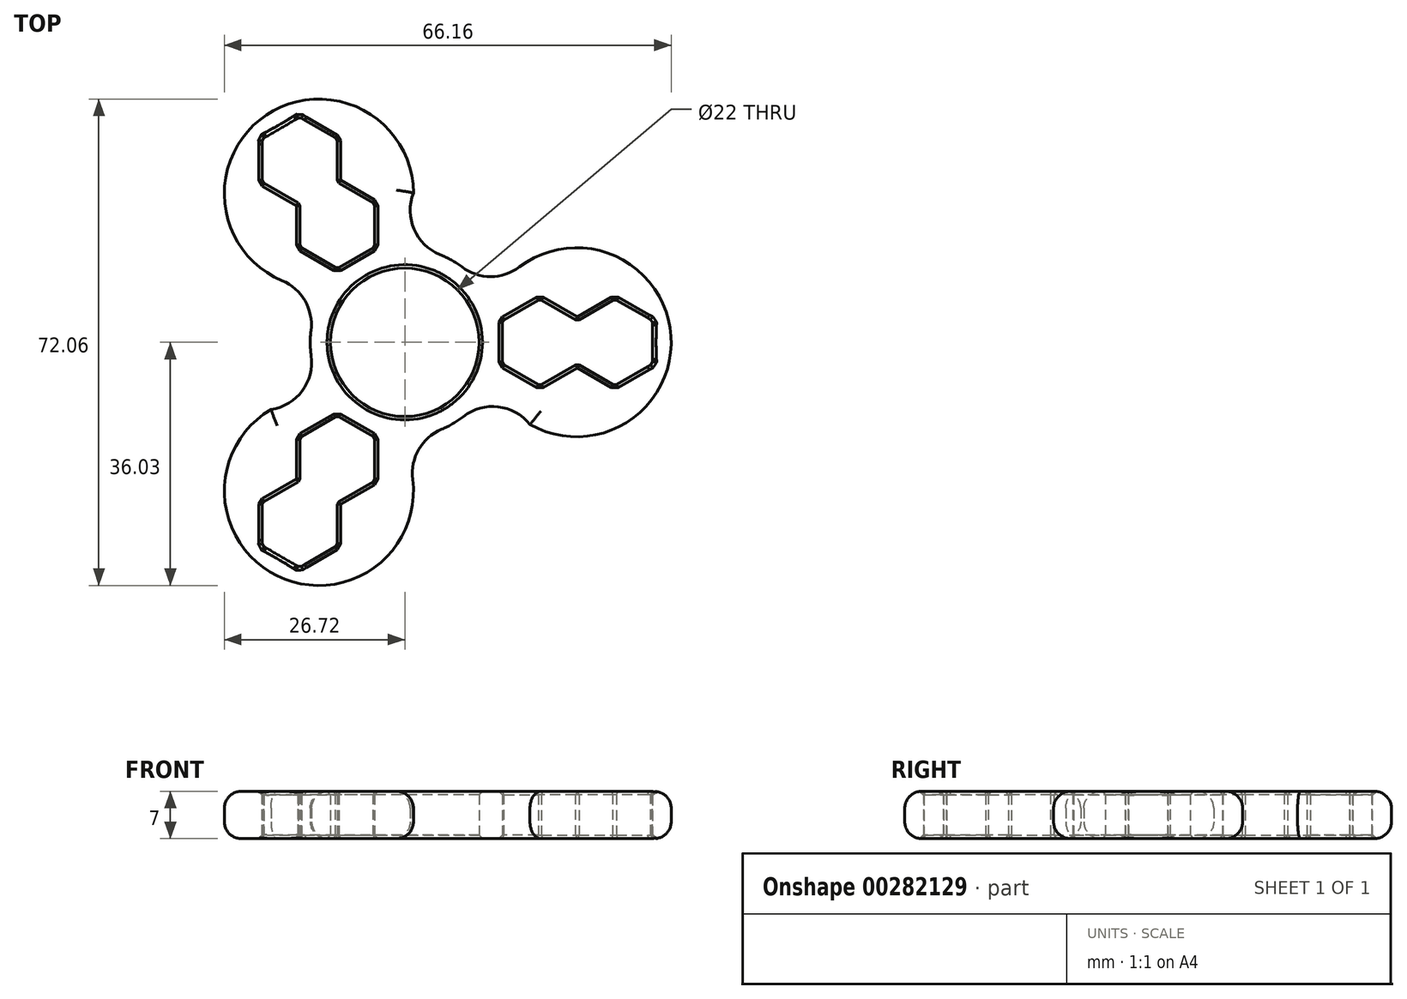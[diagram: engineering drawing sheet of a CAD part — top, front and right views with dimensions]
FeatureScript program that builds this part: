
annotation { "Feature Type Name" : "Feature", "Feature Type Description" : "" }
export const myFeature = defineFeature(function(context is Context, id is Id, definition is map)
    precondition{}
    {
        {
            var Q0;
            Q0=qCreatedBy(makeId("Top.planeOp"),FACE);
            var sketch = newSketch(context, id + "F0", { "sketchPlane" : qUnion([Q0])});
            skCircle(sketch, "E0", {"center": v(0, 0) * mm, "radius": 11 * mm});
            skCircle(sketch, "E1", {"center": v(0, 0) * mm, "radius": 14 * mm});
            skCircle(sketch, "E2", {"center": v(25.44, 0) * mm, "radius": 14 * mm});
            skArc(sketch, "E3", {"start": v(18.93, 13.42) * mm, "mid": v(12.38, 9.74) * mm, "end": v(6.21, 14.03) * mm});
            skArc(sketch, "E4.MirrorCS", {"start": v(19.21, -13.2) * mm, "mid": v(12.66, -9.52) * mm, "end": v(6.5, -13.81) * mm});
            skCircle(sketch, "E5.cCircle", {"center": v(31.1, 0) * mm, "radius": 6.4 * mm, "construction": true});
            skLineSegment(sketch, "E5.0", {"start": v(25.55, -3.2) * mm, "end": v(25.55, 3.2) * mm});
            skLineSegment(sketch, "E5.1", {"start": v(25.55, 3.2) * mm, "end": v(31.1, 6.4) * mm});
            skLineSegment(sketch, "E5.2", {"start": v(31.1, 6.4) * mm, "end": v(36.65, 3.2) * mm});
            skLineSegment(sketch, "E5.3", {"start": v(36.65, 3.2) * mm, "end": v(36.65, -3.2) * mm});
            skLineSegment(sketch, "E5.4", {"start": v(36.65, -3.2) * mm, "end": v(31.1, -6.4) * mm});
            skLineSegment(sketch, "E5.5", {"start": v(31.1, -6.4) * mm, "end": v(25.55, -3.2) * mm});
            skCircle(sketch, "E6.cCircle", {"center": v(20, 0) * mm, "radius": 6.4 * mm, "construction": true});
            skLineSegment(sketch, "E6.0", {"start": v(25.55, -3.2) * mm, "end": v(20, -6.4) * mm});
            skLineSegment(sketch, "E6.1", {"start": v(20, -6.4) * mm, "end": v(14.45, -3.2) * mm});
            skLineSegment(sketch, "E6.2", {"start": v(14.45, -3.2) * mm, "end": v(14.45, 3.2) * mm});
            skLineSegment(sketch, "E6.3", {"start": v(14.45, 3.2) * mm, "end": v(20, 6.4) * mm});
            skLineSegment(sketch, "E6.4", {"start": v(20, 6.4) * mm, "end": v(25.55, 3.2) * mm});
            skLineSegment(sketch, "E6.5", {"start": v(25.55, 3.2) * mm, "end": v(25.55, -3.2) * mm});
            skLineSegment(sketch, "E7", {"start": v(0, 0) * mm, "end": v(20, 0) * mm, "construction": true});
            skSolve(sketch);
        }
        {
            var Q0;
            Q0=makeQuery(id+"F0.imprint","IMPRINT",FACE,{"disambiguationData":[TD([[makeQuery(id+"F0.imprint","IMPRINT",EDGE,{"derivedFrom":sQuery(id+"F0.wireOp",EDGE,"E0")}),-1.0]])]});
            var Q1;
            {var subQ0=sQuery(id+"F0.wireOp",EDGE,"E2");var subQ1=sQuery(id+"F0.wireOp",EDGE,"E1");var subQ2=makeQuery(id+"F0.imprint","INTERSECT",VERTEX,{"disambiguationData":[OD(0.0)],"derivedFrom":[subQ1,subQ0]});Q1=makeQuery(id+"F0.imprint","IMPRINT",FACE,{"disambiguationData":[TD([[makeQuery(id+"F0.imprint","IMPRINT",EDGE,{"disambiguationData":[TD([[subQ2,1.0]])],"derivedFrom":subQ1}),1.0]])]});}
            var Q2;
            Q2=makeQuery(id+"F0.imprint","IMPRINT",FACE,{"disambiguationData":[TD([[makeQuery(id+"F0.imprint","IMPRINT",EDGE,{"derivedFrom":sQuery(id+"F0.wireOp",EDGE,"E5.1")}),1.0]])]});
            extrude(context, id + "F1", {"entities" : qUnion([Q0, Q1, Q2]), "endBound" : BoundingType.SYMMETRIC, "depth" : 7 * mm});
        }
        {
            var Q0;
            {var subQ0=sQuery(id+"F0.wireOp",EDGE,"E3");var subQ1=sQuery(id+"F0.wireOp",EDGE,"E1");var subQ2=makeQuery(id+"F0.imprint","INTERSECT",VERTEX,{"derivedFrom":[subQ1,subQ0]});Q0=makeQuery(id+"F0.imprint","IMPRINT",FACE,{"disambiguationData":[TD([[makeQuery(id+"F0.imprint","IMPRINT",EDGE,{"disambiguationData":[TD([[subQ2,1.0]])],"derivedFrom":subQ1}),-1.0]])]});}
            var Q1;
            Q1=makeQuery(id+"F0.imprint","IMPRINT",FACE,{"disambiguationData":[TD([[makeQuery(id+"F0.imprint","IMPRINT",EDGE,{"derivedFrom":sQuery(id+"F0.wireOp",EDGE,"UwXqT0ap-12Z3-Fupx-mhf0-3pL9q4EJ6cQW")}),-1.0]])]});
            var Q2;
            {var subQ0=sQuery(id+"F0.wireOp",EDGE,"gSAZEsJJ-cn3l-cjJ6-9HDa-52uPBN5IA6vx");Q2=makeQuery(id+"F0.imprint","IMPRINT",FACE,{"disambiguationData":[TD([[makeQuery(id+"F0.imprint","IMPRINT",EDGE,{"derivedFrom":subQ0}),1.0]])]});}
            var Q3;
            {var subQ0=sQuery(id+"F0.wireOp",EDGE,"VPdpeA7V-GjOX-LRlJ-2Vj8-VplDRYYToLq0");Q3=makeQuery(id+"F0.imprint","IMPRINT",FACE,{"disambiguationData":[TD([[makeQuery(id+"F0.imprint","IMPRINT",EDGE,{"derivedFrom":subQ0}),1.0]])]});}
            var Q4;
            {var subQ0=sQuery(id+"F0.wireOp",EDGE,"f63044cd-322f-4f96-b824-94d15fe920c80.MirrorCS");Q4=makeQuery(id+"F0.imprint","IMPRINT",FACE,{"disambiguationData":[TD([[makeQuery(id+"F0.imprint","IMPRINT",EDGE,{"derivedFrom":subQ0}),-1.0]])]});}
            var Q5;
            {var subQ0=sQuery(id+"F0.wireOp",EDGE,"f037a777-31d1-4705-85f1-b677b52131420.MirrorCS");Q5=makeQuery(id+"F0.imprint","IMPRINT",FACE,{"disambiguationData":[TD([[makeQuery(id+"F0.imprint","IMPRINT",EDGE,{"derivedFrom":subQ0}),-1.0]])]});}
            var Q6;
            {var subQ0=sQuery(id+"F0.wireOp",EDGE,"a2668e3b-8a0b-417b-9202-db38daa61a800.MirrorCS");Q6=makeQuery(id+"F0.imprint","IMPRINT",FACE,{"disambiguationData":[TD([[makeQuery(id+"F0.imprint","IMPRINT",EDGE,{"derivedFrom":subQ0}),-1.0]])]});}
            var Q7;
            {var subQ0=sQuery(id+"F0.wireOp",EDGE,"diWcMJ20-Xh2n-FcUL-icb3-4419BL6dKp2H");Q7=makeQuery(id+"F0.imprint","IMPRINT",FACE,{"disambiguationData":[TD([[makeQuery(id+"F0.imprint","IMPRINT",EDGE,{"derivedFrom":subQ0}),1.0]])]});}
            var Q8;
            {var subQ0=sQuery(id+"F0.wireOp",EDGE,"E4.MirrorCS");var subQ1=sQuery(id+"F0.wireOp",EDGE,"E1");var subQ2=makeQuery(id+"F0.imprint","INTERSECT",VERTEX,{"derivedFrom":[subQ1,subQ0]});Q8=makeQuery(id+"F0.imprint","IMPRINT",FACE,{"disambiguationData":[TD([[makeQuery(id+"F0.imprint","IMPRINT",EDGE,{"disambiguationData":[TD([[subQ2,-1.0]])],"derivedFrom":subQ1}),-1.0]])]});}
            extrude(context, id + "F2", {"entities" : qUnion([Q0, Q1, Q2, Q3, Q4, Q5, Q6, Q7, Q8]), "operationType" : NewBodyOperationType.ADD, "endBound" : BoundingType.SYMMETRIC, "depth" : 7 * mm});
        }
        {
            var Q0;
            Q0=makeQuery(id+"F2.opExtrude","CAP_EDGE",EDGE,{"disambiguationData":[OSD([sQuery(id+"F0.wireOp",EDGE,"E3")])],"isStart":false});
            var Q1;
            Q1=makeQuery(id+"F2.opExtrude","CAP_EDGE",EDGE,{"disambiguationData":[OSD([sQuery(id+"F0.wireOp",EDGE,"gSAZEsJJ-cn3l-cjJ6-9HDa-52uPBN5IA6vx")])],"isStart":false});
            var Q2;
            Q2=makeQuery(id+"F2.opExtrude","CAP_EDGE",EDGE,{"disambiguationData":[OSD([sQuery(id+"F0.wireOp",EDGE,"VPdpeA7V-GjOX-LRlJ-2Vj8-VplDRYYToLq0")])],"isStart":false});
            var Q3;
            Q3=makeQuery(id+"F2.opExtrude","CAP_EDGE",EDGE,{"disambiguationData":[OSD([sQuery(id+"F0.wireOp",EDGE,"diWcMJ20-Xh2n-FcUL-icb3-4419BL6dKp2H")])],"isStart":false});
            var Q4;
            Q4=makeQuery(id+"F2.opExtrude","CAP_EDGE",EDGE,{"disambiguationData":[OSD([sQuery(id+"F0.wireOp",EDGE,"a2668e3b-8a0b-417b-9202-db38daa61a800.MirrorCS")])],"isStart":false});
            var Q5;
            Q5=makeQuery(id+"F2.opExtrude","CAP_EDGE",EDGE,{"disambiguationData":[OSD([sQuery(id+"F0.wireOp",EDGE,"f037a777-31d1-4705-85f1-b677b52131420.MirrorCS")])],"isStart":false});
            var Q6;
            Q6=makeQuery(id+"F2.opExtrude","CAP_EDGE",EDGE,{"disambiguationData":[OSD([sQuery(id+"F0.wireOp",EDGE,"f63044cd-322f-4f96-b824-94d15fe920c80.MirrorCS")])],"isStart":false});
            var Q7;
            Q7=makeQuery(id+"F2.opExtrude","CAP_EDGE",EDGE,{"disambiguationData":[OSD([sQuery(id+"F0.wireOp",EDGE,"E4.MirrorCS")])],"isStart":false});
            var Q8;
            Q8=makeQuery(id+"F2.opExtrude","CAP_EDGE",EDGE,{"disambiguationData":[OSD([sQuery(id+"F0.wireOp",EDGE,"E3")])],"isStart":true});
            var Q9;
            Q9=makeQuery(id+"F2.opExtrude","CAP_EDGE",EDGE,{"disambiguationData":[OSD([sQuery(id+"F0.wireOp",EDGE,"E4.MirrorCS")])],"isStart":true});
            var Q10;
            Q10=makeQuery(id+"F2.opExtrude","CAP_EDGE",EDGE,{"disambiguationData":[OSD([sQuery(id+"F0.wireOp",EDGE,"gSAZEsJJ-cn3l-cjJ6-9HDa-52uPBN5IA6vx")])],"isStart":true});
            var Q11;
            Q11=makeQuery(id+"F2.opExtrude","CAP_EDGE",EDGE,{"disambiguationData":[OSD([sQuery(id+"F0.wireOp",EDGE,"VPdpeA7V-GjOX-LRlJ-2Vj8-VplDRYYToLq0")])],"isStart":true});
            var Q12;
            Q12=makeQuery(id+"F2.opExtrude","CAP_EDGE",EDGE,{"disambiguationData":[OSD([sQuery(id+"F0.wireOp",EDGE,"diWcMJ20-Xh2n-FcUL-icb3-4419BL6dKp2H")])],"isStart":true});
            var Q13;
            Q13=makeQuery(id+"F2.opExtrude","CAP_EDGE",EDGE,{"disambiguationData":[OSD([sQuery(id+"F0.wireOp",EDGE,"a2668e3b-8a0b-417b-9202-db38daa61a800.MirrorCS")])],"isStart":true});
            var Q14;
            Q14=makeQuery(id+"F2.opExtrude","CAP_EDGE",EDGE,{"disambiguationData":[OSD([sQuery(id+"F0.wireOp",EDGE,"f037a777-31d1-4705-85f1-b677b52131420.MirrorCS")])],"isStart":true});
            var Q15;
            Q15=makeQuery(id+"F2.opExtrude","CAP_EDGE",EDGE,{"disambiguationData":[OSD([sQuery(id+"F0.wireOp",EDGE,"f63044cd-322f-4f96-b824-94d15fe920c80.MirrorCS")])],"isStart":true});
            fillet(context, id + "F3", {"entities" : qUnion([Q0, Q1, Q2, Q3, Q4, Q5, Q6, Q7, Q8, Q9, Q10, Q11, Q12, Q13, Q14, Q15]), "radius" : 2.5 * mm, "tangentPropagation" : true, "allowEdgeOverflow" : false});
        }
        {
            var Q0;
            Q0=makeQuery(id+"F1.opExtrude","SWEPT_FACE",FACE,{"disambiguationData":[OSD([sQuery(id+"F0.wireOp",EDGE,"E0")])]});
            var Q1;
            Q1=makeQuery(id+"F1.opExtrude","CAP_EDGE",EDGE,{"disambiguationData":[OSD([sQuery(id+"F0.wireOp",EDGE,"E6.3")])],"isStart":false});
            var Q2;
            Q2=makeQuery(id+"F1.opExtrude","CAP_EDGE",EDGE,{"disambiguationData":[OSD([sQuery(id+"F0.wireOp",EDGE,"E6.4")])],"isStart":false});
            var Q3;
            Q3=makeQuery(id+"F1.opExtrude","CAP_EDGE",EDGE,{"disambiguationData":[OSD([sQuery(id+"F0.wireOp",EDGE,"E5.1")])],"isStart":false});
            var Q4;
            Q4=makeQuery(id+"F1.opExtrude","CAP_EDGE",EDGE,{"disambiguationData":[OSD([sQuery(id+"F0.wireOp",EDGE,"E5.2")])],"isStart":false});
            var Q5;
            {var subQ0=sQuery(id+"F0.wireOp",EDGE,"E2");var subQ1=makeQuery(id+"F0.imprint","INTERSECT",VERTEX,{"derivedFrom":[subQ0,sQuery(id+"F0.wireOp",EDGE,"E3")]});Q5=makeQuery(id+"F3.opFillet","BLEND_EDGE",EDGE,{"blendedFrom":[makeQuery(id+"F1.opExtrude","CAP_EDGE",EDGE,{"disambiguationData":[OSD([subQ0]),TDD([makeQuery(id+"F0.imprint","IMPRINT",EDGE,{"disambiguationData":[TD([[subQ1,-1.0]])],"derivedFrom":subQ0}),makeQuery(id+"F0.imprint","IMPRINT",EDGE,{"disambiguationData":[TD([[subQ1,1.0]])],"derivedFrom":subQ0})])],"isStart":false}),makeQuery(id+"F1.opExtrude","SWEPT_FACE",FACE,{"disambiguationData":[OSD([sQuery(id+"F0.wireOp",EDGE,"E5.3")])]})],"blendedInto":[makeQuery(id+"F1.opExtrude","SWEPT_FACE",FACE,{"disambiguationData":[OSD([sQuery(id+"F0.wireOp",EDGE,"E5.3")])]})]});}
            var Q6;
            Q6=makeQuery(id+"F1.opExtrude","CAP_EDGE",EDGE,{"disambiguationData":[OSD([sQuery(id+"F0.wireOp",EDGE,"E5.4")])],"isStart":false});
            var Q7;
            Q7=makeQuery(id+"F1.opExtrude","CAP_EDGE",EDGE,{"disambiguationData":[OSD([sQuery(id+"F0.wireOp",EDGE,"E5.5")])],"isStart":false});
            var Q8;
            Q8=makeQuery(id+"F1.opExtrude","CAP_EDGE",EDGE,{"disambiguationData":[OSD([sQuery(id+"F0.wireOp",EDGE,"E6.0")])],"isStart":false});
            var Q9;
            Q9=makeQuery(id+"F1.opExtrude","CAP_EDGE",EDGE,{"disambiguationData":[OSD([sQuery(id+"F0.wireOp",EDGE,"E6.1")])],"isStart":false});
            var Q10;
            Q10=makeQuery(id+"F1.opExtrude","CAP_EDGE",EDGE,{"disambiguationData":[OSD([sQuery(id+"F0.wireOp",EDGE,"E6.2")])],"isStart":false});
            var Q11;
            Q11=makeQuery(id+"F1.opExtrude","CAP_EDGE",EDGE,{"disambiguationData":[OSD([sQuery(id+"F0.wireOp",EDGE,"E5.1")])],"isStart":true});
            var Q12;
            Q12=makeQuery(id+"F1.opExtrude","SWEPT_FACE",FACE,{"disambiguationData":[OSD([sQuery(id+"F0.wireOp",EDGE,"E5.2")])]});
            var Q13;
            Q13=makeQuery(id+"F1.opExtrude","SWEPT_FACE",FACE,{"disambiguationData":[OSD([sQuery(id+"F0.wireOp",EDGE,"E5.4")])]});
            var Q14;
            Q14=makeQuery(id+"F1.opExtrude","SWEPT_FACE",FACE,{"disambiguationData":[OSD([sQuery(id+"F0.wireOp",EDGE,"E6.0")])]});
            var Q15;
            Q15=makeQuery(id+"F1.opExtrude","SWEPT_FACE",FACE,{"disambiguationData":[OSD([sQuery(id+"F0.wireOp",EDGE,"E6.1")])]});
            var Q16;
            Q16=makeQuery(id+"F1.opExtrude","SWEPT_FACE",FACE,{"disambiguationData":[OSD([sQuery(id+"F0.wireOp",EDGE,"E6.2")])]});
            var Q17;
            Q17=makeQuery(id+"F1.opExtrude","SWEPT_FACE",FACE,{"disambiguationData":[OSD([sQuery(id+"F0.wireOp",EDGE,"E6.4")])]});
            chamfer(context, id + "F4", {"entities" : qUnion([Q0, Q1, Q2, Q3, Q4, Q5, Q6, Q7, Q8, Q9, Q10, Q11, Q12, Q13, Q14, Q15, Q16, Q17]), "width" : .5 * mm, "tangentPropagation" : true});
        }
        {
            var Q0;
            Q0=makeQuery(id+"F1.opExtrude","SWEPT_BODY",BODY,{"disambiguationData":[OSD([sQuery(id+"F0.wireOp",EDGE,"E0"),sQuery(id+"F0.wireOp",EDGE,"E1"),sQuery(id+"F0.wireOp",EDGE,"UwXqT0ap-12Z3-Fupx-mhf0-3pL9q4EJ6cQW"),sQuery(id+"F0.wireOp",EDGE,"E3"),sQuery(id+"F0.wireOp",EDGE,"E4.MirrorCS"),sQuery(id+"F0.wireOp",EDGE,"gSAZEsJJ-cn3l-cjJ6-9HDa-52uPBN5IA6vx"),sQuery(id+"F0.wireOp",EDGE,"VPdpeA7V-GjOX-LRlJ-2Vj8-VplDRYYToLq0"),sQuery(id+"F0.wireOp",EDGE,"diWcMJ20-Xh2n-FcUL-icb3-4419BL6dKp2H"),sQuery(id+"F0.wireOp",EDGE,"f63044cd-322f-4f96-b824-94d15fe920c80.MirrorCS"),sQuery(id+"F0.wireOp",EDGE,"f037a777-31d1-4705-85f1-b677b52131420.MirrorCS"),sQuery(id+"F0.wireOp",EDGE,"a2668e3b-8a0b-417b-9202-db38daa61a800.MirrorCS")])]});
            var Q1;
            Q1=makeQuery(id+"F1.opExtrude","SWEPT_FACE",FACE,{"disambiguationData":[OSD([sQuery(id+"F0.wireOp",EDGE,"E0")])]});
            circularPattern(context, id + "F5", {"operationType" : NewBodyOperationType.ADD, "entities" : qUnion([Q0]), "axis" : qUnion([Q1]), "angle" : 360 * degree, "instanceCount" : 3, "equalSpace" : true});
        }
    });
